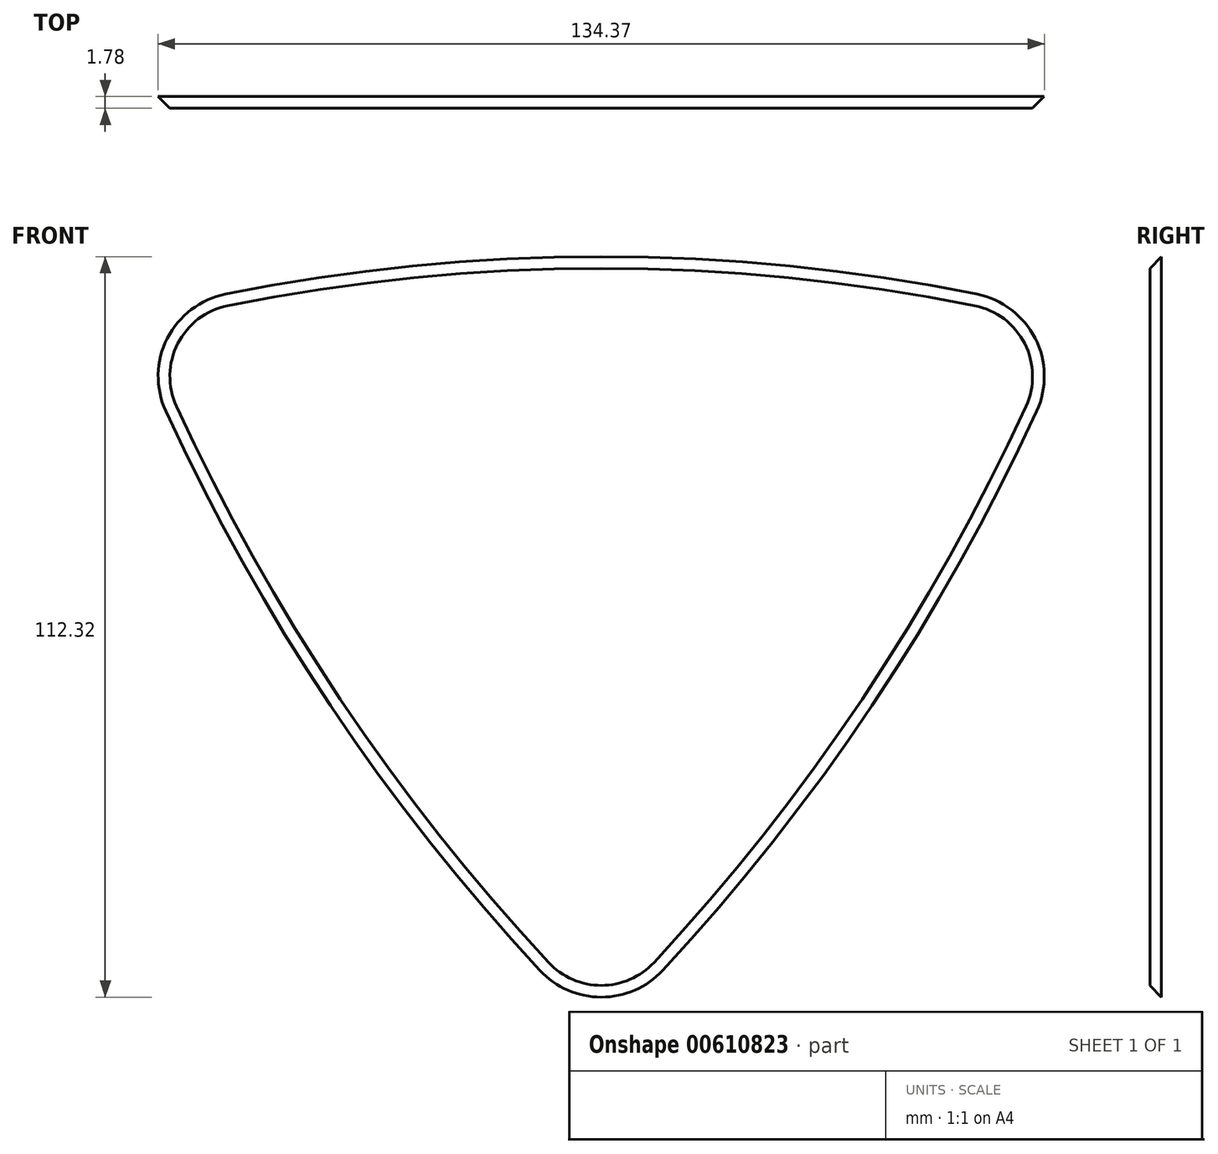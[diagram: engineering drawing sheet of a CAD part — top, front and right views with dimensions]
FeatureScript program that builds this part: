
annotation { "Feature Type Name" : "Feature", "Feature Type Description" : "" }
export const myFeature = defineFeature(function(context is Context, id is Id, definition is map)
    precondition{}
    {
        {
            var Q0;
            Q0=qCreatedBy(makeId("Front.planeOp"),FACE);
            var sketch = newSketch(context, id + "F0", { "sketchPlane" : qUnion([Q0])});
            skLineSegment(sketch, "E0", {"start": v(0, 43.15) * mm, "end": v(0, 42.67) * mm});
            skLineSegment(sketch, "E1", {"start": v(0, -49.73) * mm, "end": v(0, -48.71) * mm});
            skPoint(sketch, "E2.orphan", {"position": v(-43.6, -52.52) * mm});
            skPoint(sketch, "E3.orphan", {"position": v(43.1, -52.52) * mm});
            skArc(sketch, "E4.0", {"start": v(56.99, 47.18) * mm, "mid": v(0, 52.87) * mm, "end": v(-57, 47.18) * mm});
            skArc(sketch, "E5.0", {"start": v(-57, 47.18) * mm, "mid": v(-65.8, 40.49) * mm, "end": v(-66.03, 29.43) * mm});
            skArc(sketch, "E5.1", {"start": v(-9.3, -55.4) * mm, "mid": v(0, -59.45) * mm, "end": v(9.3, -55.4) * mm});
            skArc(sketch, "E5.2", {"start": v(9.3, -55.4) * mm, "mid": v(41.04, -15.24) * mm, "end": v(66.02, 29.43) * mm});
            skArc(sketch, "E5.3", {"start": v(-66.03, 29.43) * mm, "mid": v(-41.05, -15.24) * mm, "end": v(-9.3, -55.4) * mm});
            skArc(sketch, "E5.4", {"start": v(66.02, 29.43) * mm, "mid": v(65.8, 40.49) * mm, "end": v(56.99, 47.18) * mm});
            skSolve(sketch);
        }
        {
            var Q0;
            Q0=makeQuery(id+"F0.imprint","IMPRINT",FACE,{"disambiguationData":[TD([[makeQuery(id+"F0.imprint","IMPRINT",EDGE,{"derivedFrom":sQuery(id+"F0.wireOp",EDGE,"E5.0")}),1.0]])]});
            extrude(context, id + "F1", {"entities" : qUnion([Q0]), "depth" : 1.78 * mm, "offsetDistance" : 25.4 * mm});
        }
        {
            var Q0;
            Q0=makeQuery(id+"F1.opExtrude","CAP_EDGE",EDGE,{"disambiguationData":[OSD([sQuery(id+"F0.wireOp",EDGE,"E5.3")])],"isStart":false});
            chamfer(context, id + "F2", {"entities" : qUnion([Q0]), "width" : 1.78 * mm, "tangentPropagation" : true});
        }
    });
